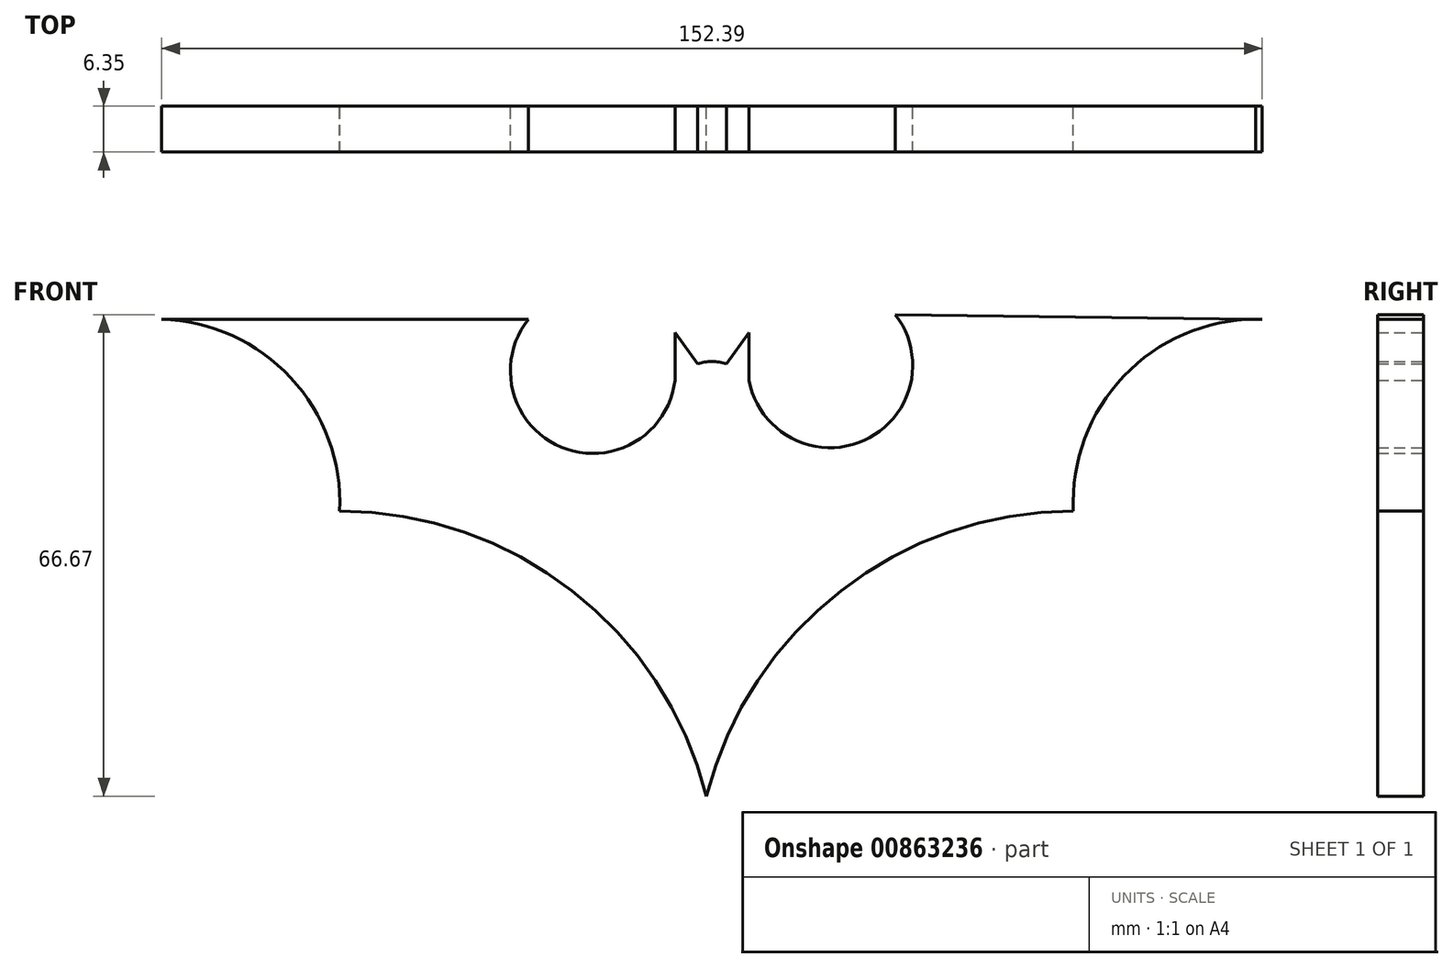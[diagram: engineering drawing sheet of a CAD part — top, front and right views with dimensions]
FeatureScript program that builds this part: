
annotation { "Feature Type Name" : "Feature", "Feature Type Description" : "" }
export const myFeature = defineFeature(function(context is Context, id is Id, definition is map)
    precondition{}
    {
        {
            var Q0;
            Q0=qCreatedBy(makeId("Front.planeOp"),FACE);
            var sketch = newSketch(context, id + "F0", { "sketchPlane" : qUnion([Q0])});
            skLineSegment(sketch, "E0", {"start": v(-82.8, 12.17) * mm, "end": v(-32, 12.17) * mm});
            skArc(sketch, "E1", {"start": v(-58.16, -14.38) * mm, "mid": v(-64.92, 4.06) * mm, "end": v(-82.8, 12.17) * mm});
            skLineSegment(sketch, "E2", {"start": v(-58.16, -14.38) * mm, "end": v(-7.36, -14.38) * mm, "construction": true});
            skArc(sketch, "E3", {"start": v(69.6, 12.16) * mm, "mid": v(50.73, 4.6) * mm, "end": v(43.44, -14.38) * mm});
            skLineSegment(sketch, "E4", {"start": v(-7.36, -14.38) * mm, "end": v(43.44, -14.38) * mm, "construction": true});
            skLineSegment(sketch, "E5", {"start": v(-6.6, 12.16) * mm, "end": v(-7.36, -53.86) * mm, "construction": true});
            skArc(sketch, "E6", {"start": v(-7.36, -53.86) * mm, "mid": v(-25.99, -25.4) * mm, "end": v(-58.16, -14.38) * mm});
            skArc(sketch, "E7", {"start": v(43.44, -14.38) * mm, "mid": v(11.27, -25.4) * mm, "end": v(-7.36, -53.86) * mm});
            skLineSegment(sketch, "E8", {"start": v(18.8, 12.81) * mm, "end": v(69.6, 12.16) * mm});
            skLineSegment(sketch, "E9", {"start": v(-32, 12.17) * mm, "end": v(-32, -3.05) * mm, "construction": true});
            skLineSegment(sketch, "E10", {"start": v(18.8, 12.81) * mm, "end": v(18.8, 12.81) * mm});
            skLineSegment(sketch, "E11", {"start": v(18.8, -3.05) * mm, "end": v(6.1, -3.05) * mm, "construction": true});
            skLineSegment(sketch, "E12", {"start": v(-19.3, -3.05) * mm, "end": v(-32, -3.05) * mm, "construction": true});
            skLineSegment(sketch, "E13", {"start": v(6.1, -3.05) * mm, "end": v(-19.3, -3.05) * mm});
            skLineSegment(sketch, "E14", {"start": v(18.8, 12.81) * mm, "end": v(18.8, -3.05) * mm, "construction": true});
            skLineSegment(sketch, "E15", {"start": v(-11.73, 3.72) * mm, "end": v(-1.47, 3.72) * mm});
            skArc(sketch, "E16", {"start": v(-1.47, 3.72) * mm, "mid": v(-6.6, 6.33) * mm, "end": v(-11.73, 3.72) * mm});
            skLineSegment(sketch, "E17", {"start": v(-11.73, 3.72) * mm, "end": v(-11.73, 10.33) * mm});
            skLineSegment(sketch, "E18", {"start": v(-11.73, 10.33) * mm, "end": v(-8.6, 6) * mm});
            skLineSegment(sketch, "E19", {"start": v(-1.47, 3.72) * mm, "end": v(-1.47, 10.33) * mm});
            skLineSegment(sketch, "E20", {"start": v(-1.47, 10.33) * mm, "end": v(-4.6, 6) * mm});
            skArc(sketch, "E21", {"start": v(-32, 12.17) * mm, "mid": v(-27.48, -5.53) * mm, "end": v(-11.73, 3.72) * mm});
            skArc(sketch, "E22", {"start": v(-1.47, 3.72) * mm, "mid": v(14.44, -4.62) * mm, "end": v(18.8, 12.81) * mm});
            skSolve(sketch);
        }
        {
            var Q0;
            Q0 = qSketchRegion(id + "F0", true);
            extrude(context, id + "F1", {"entities" : qUnion([Q0]), "depth" : 6.35 * mm, "offsetDistance" : 25.4 * mm});
        }
    });
